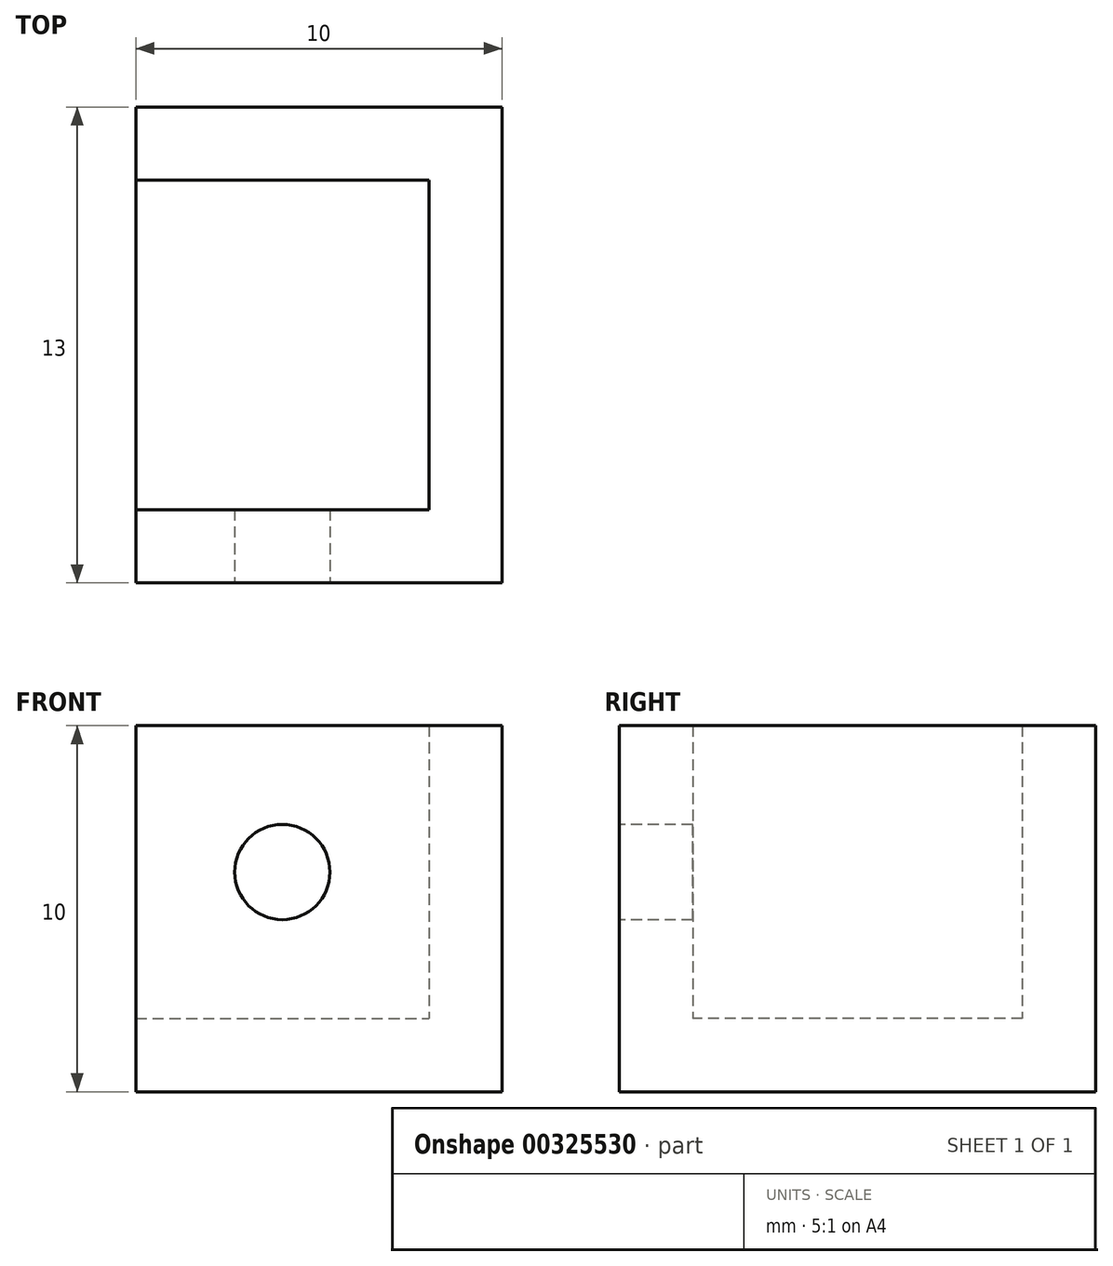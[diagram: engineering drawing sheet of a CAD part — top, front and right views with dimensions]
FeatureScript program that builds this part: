
annotation { "Feature Type Name" : "Feature", "Feature Type Description" : "" }
export const myFeature = defineFeature(function(context is Context, id is Id, definition is map)
    precondition{}
    {
        {
            var Q0;
            Q0=qCreatedBy(makeId("Top.planeOp"),FACE);
            var sketch = newSketch(context, id + "F0", { "sketchPlane" : qUnion([Q0])});
            skLineSegment(sketch, "E0.bottom", {"start": v(5, -6.5) * mm, "end": v(-5, -6.5) * mm});
            skLineSegment(sketch, "E0.top", {"start": v(5, 6.5) * mm, "end": v(-5, 6.5) * mm});
            skLineSegment(sketch, "E0.left", {"start": v(5, -6.5) * mm, "end": v(5, 6.5) * mm});
            skLineSegment(sketch, "E0.right", {"start": v(-5, -6.5) * mm, "end": v(-5, 6.5) * mm});
            skPoint(sketch, "E0.middle", {"position": v(0, 0) * mm});
            skLineSegment(sketch, "E1.bottom", {"start": v(3, -4.5) * mm, "end": v(-3, -4.5) * mm});
            skLineSegment(sketch, "E1.top", {"start": v(3, 4.5) * mm, "end": v(-3, 4.5) * mm});
            skLineSegment(sketch, "E1.left", {"start": v(3, -4.5) * mm, "end": v(3, 4.5) * mm});
            skLineSegment(sketch, "E1.right", {"start": v(-3, -4.5) * mm, "end": v(-3, 4.5) * mm});
            skLineSegment(sketch, "E2", {"start": v(-3, 4.5) * mm, "end": v(-5, 4.5) * mm});
            skLineSegment(sketch, "E3", {"start": v(-3, -4.5) * mm, "end": v(-5, -4.5) * mm});
            skSolve(sketch);
        }
        {
            var Q0;
            {var subQ1=sQuery(id+"F0.wireOp",EDGE,"E0.bottom");Q0=makeQuery(id+"F0.imprint","IMPRINT",FACE,{"disambiguationData":[TD([[makeQuery(id+"F0.imprint","IMPRINT",EDGE,{"derivedFrom":subQ1}),-1.0]])]});}
            extrude(context, id + "F1", {"entities" : qUnion([Q0]), "depth" : 10 * mm});
        }
        {
            var Q0;
            Q0=makeQuery(id+"F1.opExtrude","SWEPT_FACE",FACE,{"disambiguationData":[OSD([sQuery(id+"F0.wireOp",EDGE,"E1.left")])]});
            var sketch = newSketch(context, id + "F2", { "sketchPlane" : qUnion([Q0])});
            skLineSegment(sketch, "E4.0.0", {"start": v(-4.5, 0) * mm, "end": v(4.5, 0) * mm});
            skLineSegment(sketch, "E4.0.1", {"start": v(4.5, 0) * mm, "end": v(4.5, 10) * mm});
            skLineSegment(sketch, "E4.0.2", {"start": v(4.5, 10) * mm, "end": v(-4.5, 10) * mm});
            skLineSegment(sketch, "E4.0.3", {"start": v(-4.5, 10) * mm, "end": v(-4.5, 0) * mm});
            skPoint(sketch, "E5", {"position": v(-4.5, 2) * mm});
            skLineSegment(sketch, "E6", {"start": v(-4.5, 2) * mm, "end": v(4.5, 2) * mm});
            skSolve(sketch);
        }
        {
            var Q0;
            {var subQ0=sQuery(id+"F2.wireOp",EDGE,"E4.0.0");Q0=makeQuery(id+"F2.imprint","IMPRINT",FACE,{"disambiguationData":[TD([[makeQuery(id+"F2.imprint","IMPRINT",EDGE,{"derivedFrom":subQ0}),-1.0]])]});}
            extrude(context, id + "F3", {"entities" : qUnion([Q0]), "operationType" : NewBodyOperationType.ADD, "depth" : 8 * mm});
        }
        {
            var Q0;
            Q0=makeQuery(id+"F1.opExtrude","SWEPT_FACE",FACE,{"disambiguationData":[OSD([sQuery(id+"F0.wireOp",EDGE,"E0.bottom")])]});
            var sketch = newSketch(context, id + "F4", { "sketchPlane" : qUnion([Q0])});
            skLineSegment(sketch, "E7.0.0", {"start": v(-5, 0) * mm, "end": v(5, 0) * mm});
            skLineSegment(sketch, "E7.0.1", {"start": v(5, 0) * mm, "end": v(5, 10) * mm});
            skLineSegment(sketch, "E7.0.2", {"start": v(5, 10) * mm, "end": v(-5, 10) * mm});
            skLineSegment(sketch, "E7.0.3", {"start": v(-5, 10) * mm, "end": v(-5, 0) * mm});
            skCircle(sketch, "E8", {"center": v(-1, 6) * mm, "radius": 1.3 * mm});
            skSolve(sketch);
        }
        {
            var Q0;
            Q0=makeQuery(id+"F4.imprint","IMPRINT",FACE,{"disambiguationData":[TD([[makeQuery(id+"F4.imprint","IMPRINT",EDGE,{"derivedFrom":sQuery(id+"F4.wireOp",EDGE,"NgOUmwW7-8U8m-MLwP-BjeM-vhEjkkgO5p01")}),1.0]])]});
            var Q1;
            Q1=makeQuery(id+"F4.imprint","IMPRINT",FACE,{"disambiguationData":[TD([[makeQuery(id+"F4.imprint","IMPRINT",EDGE,{"derivedFrom":sQuery(id+"F4.wireOp",EDGE,"E8")}),1.0]])]});
            extrude(context, id + "F5", {"entities" : qUnion([Q0, Q1]), "operationType" : NewBodyOperationType.REMOVE, "endBound" : BoundingType.UP_TO_NEXT, "oppositeDirection" : true, "depth" : 25 * mm});
        }
    });
